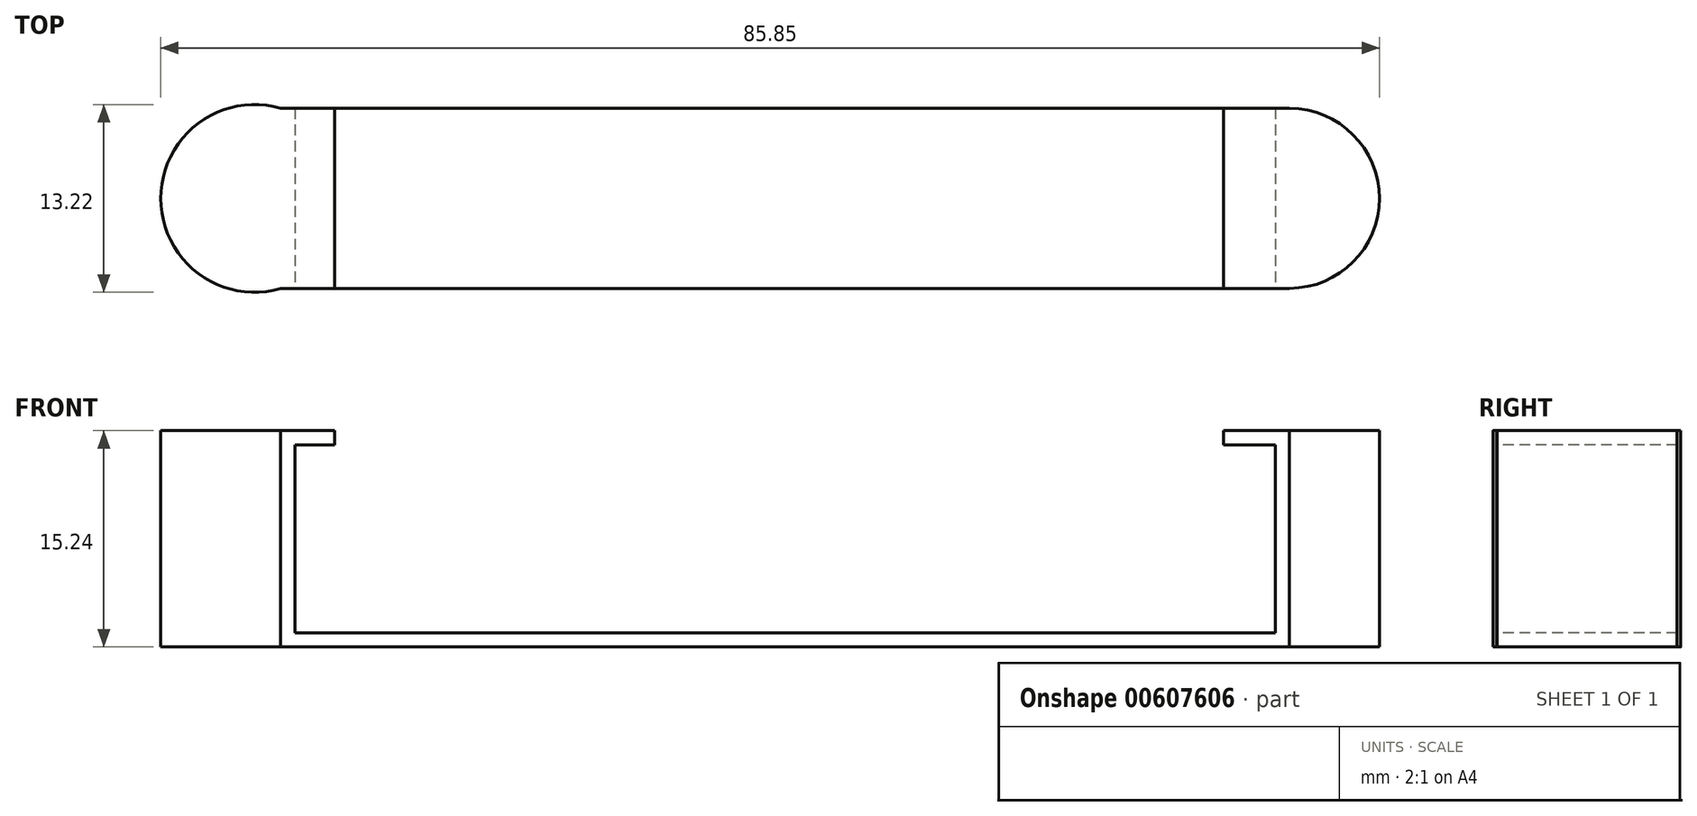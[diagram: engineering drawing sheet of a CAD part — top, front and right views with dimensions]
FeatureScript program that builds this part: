
annotation { "Feature Type Name" : "Feature", "Feature Type Description" : "" }
export const myFeature = defineFeature(function(context is Context, id is Id, definition is map)
    precondition{}
    {
        {
            var Q0;
            Q0=qCreatedBy(makeId("Top.planeOp"),FACE);
            var sketch = newSketch(context, id + "F0", { "sketchPlane" : qUnion([Q0])});
            skLineSegment(sketch, "E0", {"start": v(-28.68, 5.81) * mm, "end": v(44.22, 5.81) * mm});
            skLineSegment(sketch, "E1", {"start": v(44.22, 5.81) * mm, "end": v(44.22, 5.8) * mm});
            skLineSegment(sketch, "E2", {"start": v(44.22, -6.89) * mm, "end": v(-28.68, -6.89) * mm});
            skPoint(sketch, "E3.orphan", {"position": v(-39.29, 0) * mm});
            skArc(sketch, "E4", {"start": v(-26.84, 5.81) * mm, "mid": v(-35.29, -0.54) * mm, "end": v(-26.84, -6.89) * mm});
            skArc(sketch, "E5", {"start": v(44.22, -6.88) * mm, "mid": v(50.56, -0.54) * mm, "end": v(44.22, 5.8) * mm});
            skLineSegment(sketch, "E6.trimOffspring", {"start": v(44.22, -6.88) * mm, "end": v(44.22, -6.89) * mm});
            skSolve(sketch);
        }
        {
            var Q0;
            Q0 = qSketchRegion(id + "F0", true);
            extrude(context, id + "F1", {"entities" : qUnion([Q0]), "depth" : 15.24 * mm, "offsetDistance" : 25.4 * mm});
        }
        {
            var Q0;
            Q0=makeQuery(id+"F1.opExtrude","SWEPT_FACE",FACE,{"disambiguationData":[OSD([sQuery(id+"F0.wireOp",EDGE,"E2")])]});
            var sketch = newSketch(context, id + "F2", { "sketchPlane" : qUnion([Q0])});
            skLineSegment(sketch, "E7.0", {"start": v(-25.84, 1) * mm, "end": v(43.22, 1) * mm});
            skLineSegment(sketch, "E7.1", {"start": v(-25.84, 14.24) * mm, "end": v(-25.84, 1) * mm});
            skLineSegment(sketch, "E7.2", {"start": v(43.22, 14.24) * mm, "end": v(-25.84, 14.24) * mm});
            skLineSegment(sketch, "E7.3", {"start": v(43.22, 1) * mm, "end": v(43.22, 14.24) * mm});
            skLineSegment(sketch, "E8", {"start": v(-18.85, 14.24) * mm, "end": v(-18.85, 15.24) * mm});
            skLineSegment(sketch, "E9", {"start": v(-18.85, 15.24) * mm, "end": v(39.59, 15.24) * mm});
            skLineSegment(sketch, "E10", {"start": v(39.59, 15.24) * mm, "end": v(39.59, 14.24) * mm});
            skLineSegment(sketch, "E11", {"start": v(39.59, 14.24) * mm, "end": v(-23.05, 14.24) * mm});
            skLineSegment(sketch, "E12", {"start": v(-23.05, 14.24) * mm, "end": v(-23.05, 15.24) * mm});
            skLineSegment(sketch, "E13", {"start": v(-23.05, 15.24) * mm, "end": v(-18.85, 15.24) * mm});
            skSolve(sketch);
        }
        {
            var Q0;
            Q0 = qSketchRegion(id + "F2", true);
            extrude(context, id + "F3", {"entities" : qUnion([Q0]), "operationType" : NewBodyOperationType.REMOVE, "oppositeDirection" : true, "depth" : 25.4 * mm, "offsetDistance" : 25.4 * mm});
        }
    });
